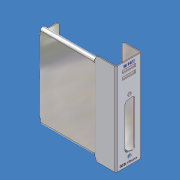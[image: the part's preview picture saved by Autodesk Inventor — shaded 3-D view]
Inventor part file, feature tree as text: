
AUTODESK INVENTOR PART (.ipt)
format: ipt  version: unknown  size: 581,120 bytes
history: native  units: mm (DEFAULTED — no unit token found)
features: sketch x12, sheet_metal_op x11, other x9, chamfer x3, extrude x1, pattern_linear x1
ambient origin geometry x8: Origin, YZ Plane, XZ Plane, XY Plane, X Axis, Y Axis, Z Axis, Center Point
feature tree (37):
  sheet_metal_op  "Face1"
  sheet_metal_op  "Flange1"
  sheet_metal_op  "Flange2"
  chamfer  "Corner Round1"
  sheet_metal_op  "Face2"
  sheet_metal_op  "Flange3"
  chamfer  "Corner Round2"
  sheet_metal_op  "Hem2"
  sheet_metal_op  "Hem3"
  chamfer  "Corner Round3"
  extrude  "Extrusion1"  Depth=80.5688mm
  pattern_linear  "Rectangular Pattern1"  Spacing1=1.778mm  [1 undecoded]
  sketch  "Sketch1"  dims[d0=22.86mm d1=80.5688mm]
  other  "Plate1"
  sketch  "Sketch2"  dims[d2=0.7874mm]
  other  "Plate2"
  sheet_metal_op  "Bend1"
  sketch  "Sketch3"  dims[d3=0.7874mm]
  other  "Plate3"
  sheet_metal_op  "Bend2"
  sketch  "Sketch4"  dims[d4=0.3937mm]
  other  "Plate4"
  sheet_metal_op  "Bend3"
  sketch  "Sketch5"  dims[d5=1.5748mm]
  other  "Plate5"
  sheet_metal_op  "Bend4"
  sketch  "Sketch8"  dims[d6=0.7874mm]
  sketch  "Sketch9"  dims[d7=16.51mm d8=90.0deg d9=0.7874mm]
  sketch  "Sketch10"  dims[d10=0.7874mm]
  sketch  "Sketch11"  dims[d11=0.3937mm]
  sketch  "Sketch12"  dims[d12=1.5748mm]
  sketch  "Sketch15"  dims[d13=0.7874mm]
  other  "Image4"
  sketch  "Sketch16"  dims[d14=17.526mm d15=90.0deg d16=0.7874mm d17=1.778mm d18=0.7874mm d19=0.7874mm d20=0.3937mm d21=1.5748mm d22=0.7874mm d23=73.66mm d24=50.8mm d25=5.08mm d26=5.08mm d27=0.7874mm d28=0.3937mm d29=1.5748mm d30=0.7874mm d31=17.78mm d32=90.0deg d33=0.7874mm d42=1.778mm d43=0.7874mm d44=0.0mm d45=0.7874mm d46=0.3937mm d47=1.5748mm d48=0.7874mm d49=3.1496mm d50=2.7432mm d51=1.3716mm d52=0.7874mm d53=0.3937mm d54=1.5748mm d55=0.7874mm d56=3.1496mm d57=2.7432mm d58=1.3716mm d59=12.7mm d60=20.32mm d62=5.588mm d63=0.7874mm d64=0.0mm d65=1.778mm d66=3.175mm d67=3.048mm d69=23.5204mm d76=30.48mm d78=0.508mm d81=-15.707963mm d94=2.54mm d95=11.43mm d96=4.064mm d97=5.588mm d98=2.54mm d99=0.0mm d100=20.0mm d102=5.0mm]
  other  "Cut1"
  other  "Cut2"
  other  "iFeature14:1"
note: 1 required parameter value undecoded (feature->parameter linkage not recoverable at this tier; creation-order binding heuristic only, values carry confidence <= 0.55)
